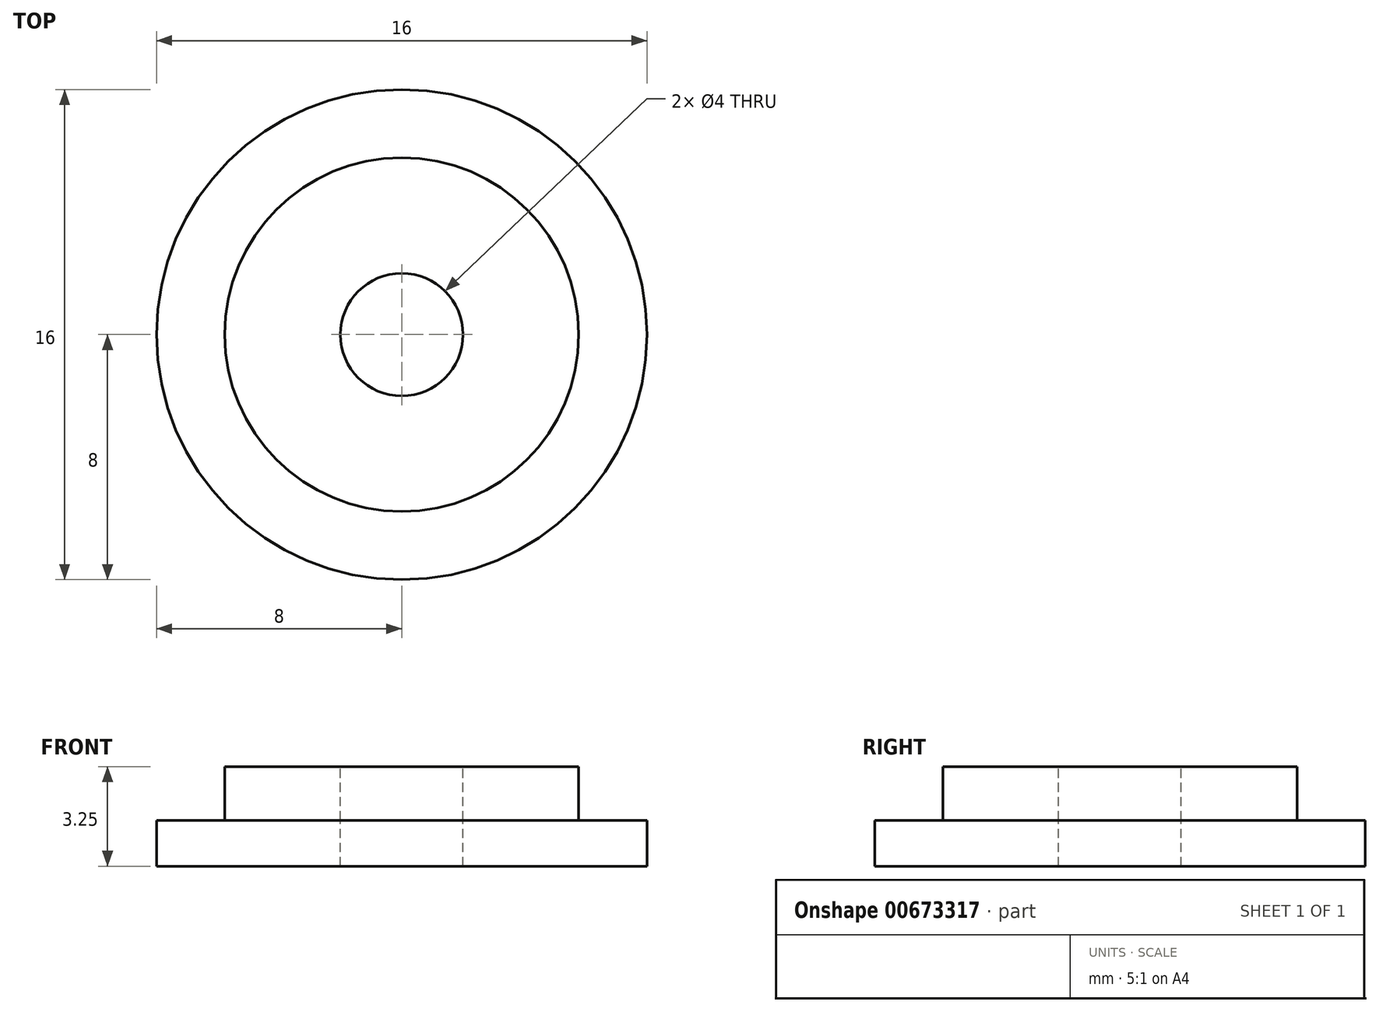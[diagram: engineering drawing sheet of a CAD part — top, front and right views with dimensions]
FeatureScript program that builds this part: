
annotation { "Feature Type Name" : "Feature", "Feature Type Description" : "" }
export const myFeature = defineFeature(function(context is Context, id is Id, definition is map)
    precondition{}
    {
        {
            var Q0;
            Q0=qCreatedBy(makeId("Top.planeOp"),FACE);
            var sketch = newSketch(context, id + "F0", { "sketchPlane" : qUnion([Q0])});
            skCircle(sketch, "E0", {"center": v(0, 0) * mm, "radius": 8 * mm});
            skSolve(sketch);
        }
        {
            var Q0;
            Q0=makeQuery(id+"F0.imprint","IMPRINT",FACE,{"disambiguationData":[TD([[makeQuery(id+"F0.imprint","IMPRINT",EDGE,{"derivedFrom":sQuery(id+"F0.wireOp",EDGE,"E0")}),1.0]])]});
            var Q1;
            Q1=sQuery(id+"F0.wireOp",EDGE,"E0");
            extrude(context, id + "F1", {"entities" : qUnion([Q0]), "surfaceEntities" : qUnion([Q1]), "depth" : 1.5 * mm, "offsetDistance" : 25 * mm});
        }
        {
            var Q0;
            Q0=makeQuery(id+"F1.opExtrude","CAP_FACE",FACE,{"disambiguationData":[OSD([sQuery(id+"F0.wireOp",EDGE,"E0")])],"isStart":false});
            var sketch = newSketch(context, id + "F2", { "sketchPlane" : qUnion([Q0])});
            skCircle(sketch, "E1", {"center": v(0, 0) * mm, "radius": 5.77 * mm});
            skSolve(sketch);
        }
        {
            var Q0;
            Q0=makeQuery(id+"F2.imprint","IMPRINT",FACE,{"disambiguationData":[TD([[makeQuery(id+"F2.imprint","IMPRINT",EDGE,{"derivedFrom":sQuery(id+"F2.wireOp",EDGE,"E1")}),1.0]])]});
            var Q1;
            Q1=sQuery(id+"F2.wireOp",EDGE,"E1");
            extrude(context, id + "F3", {"entities" : qUnion([Q0]), "surfaceEntities" : qUnion([Q1]), "depth" : 1.75 * mm, "offsetDistance" : 25 * mm});
        }
        {
            var Q0;
            Q0=makeQuery(id+"F3.opExtrude","CAP_FACE",FACE,{"disambiguationData":[OSD([sQuery(id+"F2.wireOp",EDGE,"E1")])],"isStart":false});
            var sketch = newSketch(context, id + "F4", { "sketchPlane" : qUnion([Q0])});
            skCircle(sketch, "E2", {"center": v(0, 0) * mm, "radius": 0.5 * mm});
            skSolve(sketch);
        }
        {
            var Q0;
            Q0=sQuery(id+"F4.wireOp",VERTEX,"E2.center");
            var Q1;
            Q1=makeQuery(id+"F1.opExtrude","SWEPT_BODY",BODY,{"disambiguationData":[OSD([sQuery(id+"F0.wireOp",EDGE,"E0")])]});
            var Q2;
            Q2=makeQuery(id+"F3.opExtrude","SWEPT_BODY",BODY,{"disambiguationData":[OSD([sQuery(id+"F2.wireOp",EDGE,"E1")])]});
            hole(context, id + "F5", {"style" : HoleStyle.SIMPLE, "endStyle" : HoleEndStyle.THROUGH, "holeDiameter" : 4 * mm, "majorDiameter" : 5 * mm, "isTappedThrough" : true, "tappedDepth" : 12 * mm, "tapClearance" : 3, "locations" : qUnion([Q0]), "scope" : qUnion([Q1, Q2])});
        }
    });
